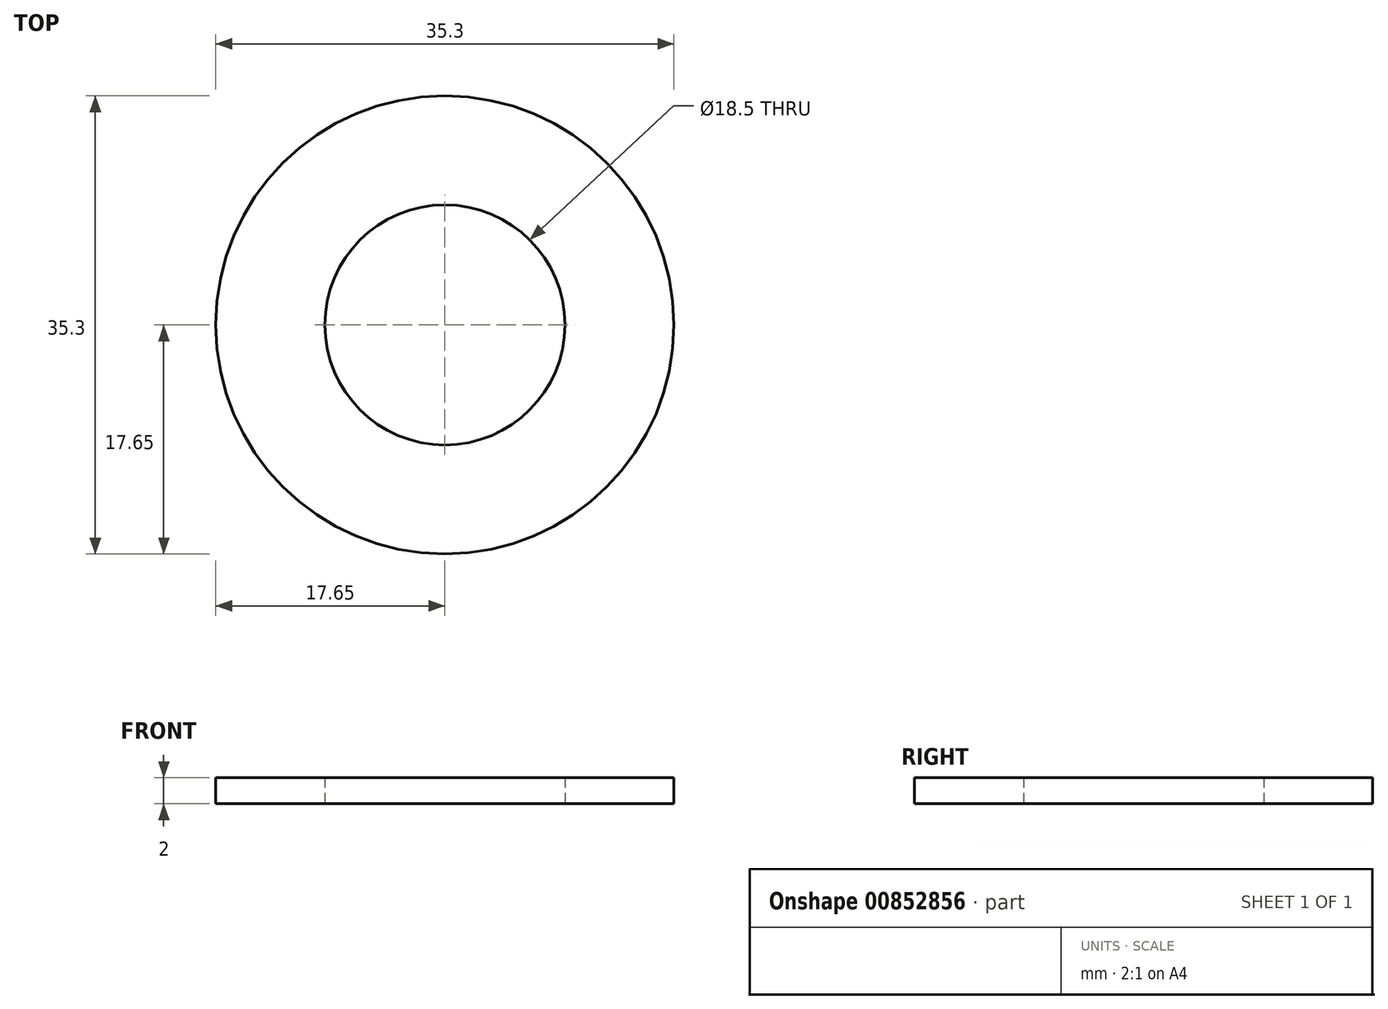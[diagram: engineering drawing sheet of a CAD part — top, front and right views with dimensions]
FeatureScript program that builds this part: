
annotation { "Feature Type Name" : "Feature", "Feature Type Description" : "" }
export const myFeature = defineFeature(function(context is Context, id is Id, definition is map)
    precondition{}
    {
        {
            var Q0;
            Q0=qCreatedBy(makeId("Top.planeOp"),FACE);
            var sketch = newSketch(context, id + "F0", { "sketchPlane" : qUnion([Q0])});
            skCircle(sketch, "E0", {"center": v(0, 0) * mm, "radius": 17.65 * mm});
            skCircle(sketch, "E1", {"center": v(0, 0) * mm, "radius": 9.25 * mm});
            skSolve(sketch);
        }
        {
            var Q0;
            Q0=makeQuery(id+"F0.imprint","IMPRINT",FACE,{"disambiguationData":[TD([[makeQuery(id+"F0.imprint","IMPRINT",EDGE,{"derivedFrom":sQuery(id+"F0.wireOp",EDGE,"E0")}),1.0]])]});
            extrude(context, id + "F1", {"entities" : qUnion([Q0]), "depth" : 2 * mm, "offsetDistance" : 25 * mm});
        }
    });
